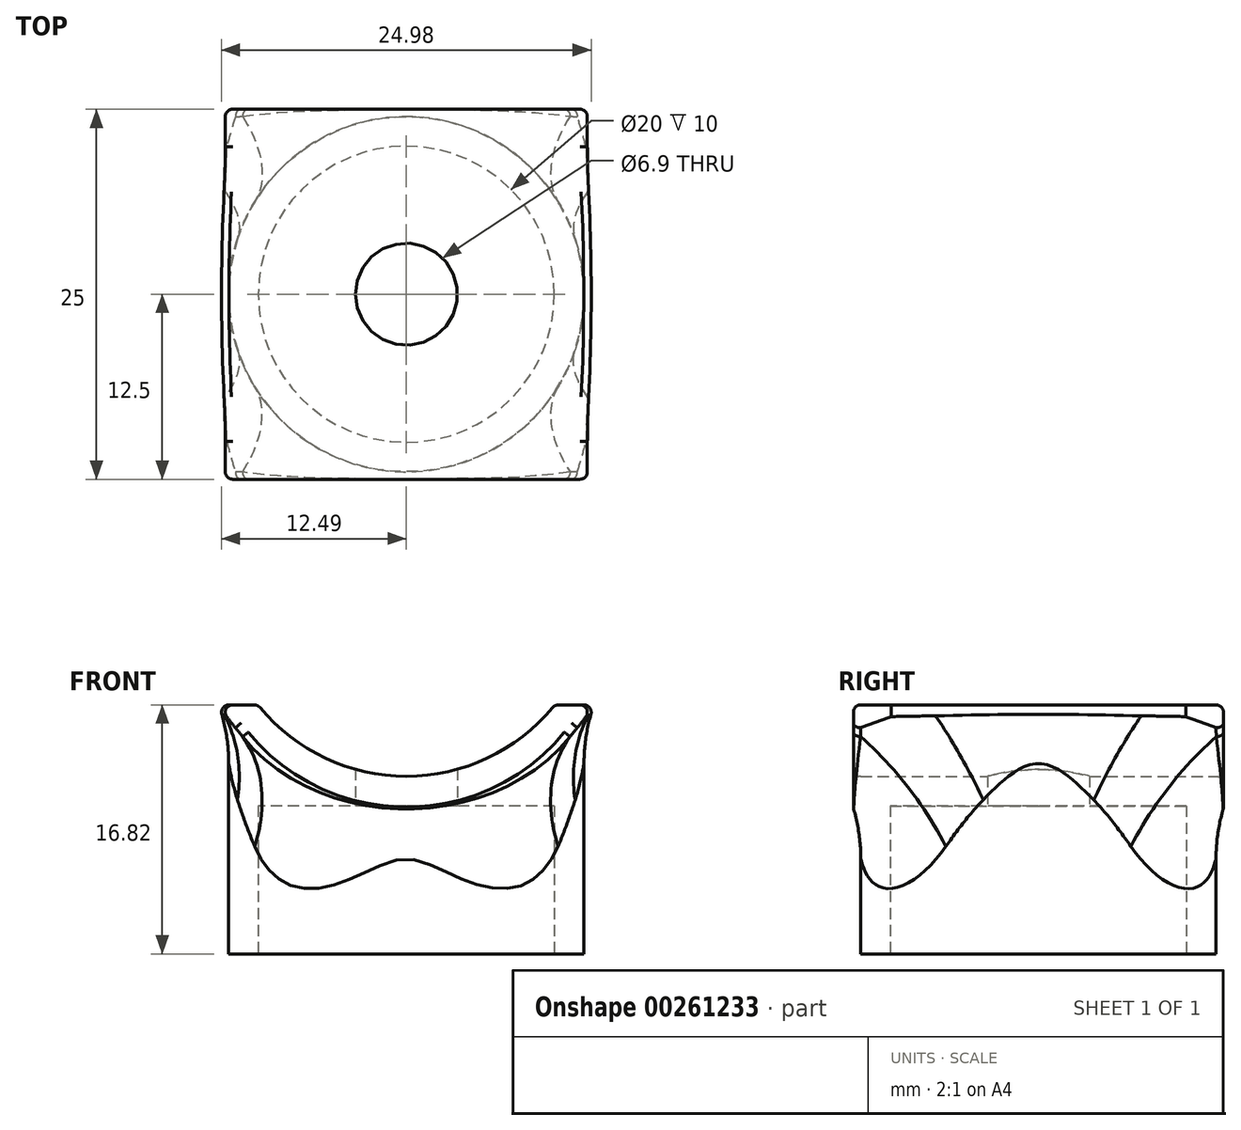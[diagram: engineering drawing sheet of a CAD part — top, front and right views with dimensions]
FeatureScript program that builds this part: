
annotation { "Feature Type Name" : "Feature", "Feature Type Description" : "" }
export const myFeature = defineFeature(function(context is Context, id is Id, definition is map)
    precondition{}
    {
        {
            var Q0;
            Q0=qCreatedBy(makeId("Top.planeOp"),FACE);
            var sketch = newSketch(context, id + "F0", { "sketchPlane" : qUnion([Q0])});
            skCircle(sketch, "E0", {"center": v(0, 0) * mm, "radius": 10 * mm});
            skCircle(sketch, "E1", {"center": v(0, 0) * mm, "radius": 12 * mm});
            skCircle(sketch, "E2", {"center": v(0, 0) * mm, "radius": 3.45 * mm});
            skSolve(sketch);
        }
        {
            var Q0;
            Q0=makeQuery(id+"F0.imprint","IMPRINT",FACE,{"disambiguationData":[TD([[makeQuery(id+"F0.imprint","IMPRINT",EDGE,{"derivedFrom":sQuery(id+"F0.wireOp",EDGE,"E0")}),-1.0]])]});
            var Q1;
            Q1=makeQuery(id+"F0.imprint","IMPRINT",FACE,{"disambiguationData":[TD([[makeQuery(id+"F0.imprint","IMPRINT",EDGE,{"derivedFrom":sQuery(id+"F0.wireOp",EDGE,"E0")}),1.0]])]});
            var Q2;
            Q2=makeQuery(id+"F0.imprint","IMPRINT",FACE,{"disambiguationData":[TD([[makeQuery(id+"F0.imprint","IMPRINT",EDGE,{"derivedFrom":sQuery(id+"F0.wireOp",EDGE,"E2")}),1.0]])]});
            extrude(context, id + "F1", {"entities" : qUnion([Q0, Q1, Q2]), "depth" : 20 * mm});
        }
        {
            var Q0;
            Q0=qCreatedBy(makeId("Front.planeOp"),FACE);
            var sketch = newSketch(context, id + "F2", { "sketchPlane" : qUnion([Q0])});
            skPoint(sketch, "E3.0", {"position": v(0, 24.85) * mm});
            skLineSegment(sketch, "E4", {"start": v(0, 0) * mm, "end": v(0, 24.85) * mm});
            skSolve(sketch);
        }
        {
            var Q0;
            Q0=qCreatedBy(makeId("Front.planeOp"),FACE);
            var sketch = newSketch(context, id + "F3", { "sketchPlane" : qUnion([Q0])});
            skPoint(sketch, "E5.0", {"position": v(0, 24.85) * mm});
            skCircle(sketch, "E6", {"center": v(0, 24.85) * mm, "radius": 12.85 * mm});
            skCircle(sketch, "E7", {"center": v(0, 24.85) * mm, "radius": 15 * mm});
            skSolve(sketch);
        }
        {
            var Q0;
            Q0=makeQuery(id+"F3.imprint","IMPRINT",FACE,{"disambiguationData":[TD([[makeQuery(id+"F3.imprint","IMPRINT",EDGE,{"derivedFrom":sQuery(id+"F3.wireOp",EDGE,"E6")}),-1.0]])]});
            extrude(context, id + "F4", {"entities" : qUnion([Q0]), "operationType" : NewBodyOperationType.ADD, "endBound" : BoundingType.SYMMETRIC, "depth" : 25 * mm});
        }
        {
            var Q0;
            Q0=qCreatedBy(makeId("Front.planeOp"),FACE);
            var sketch = newSketch(context, id + "F5", { "sketchPlane" : qUnion([Q0])});
            skCircle(sketch, "E8.0", {"center": v(0, 24.85) * mm, "radius": 12.85 * mm});
            skSolve(sketch);
        }
        {
            var Q0;
            Q0 = qSketchRegion(id + "F5", true);
            extrude(context, id + "F6", {"entities" : qUnion([Q0]), "operationType" : NewBodyOperationType.REMOVE, "endBound" : BoundingType.SYMMETRIC, "depth" : 27 * mm});
        }
        {
            var Q0;
            Q0=makeQuery(id+"F0.imprint","IMPRINT",FACE,{"disambiguationData":[TD([[makeQuery(id+"F0.imprint","IMPRINT",EDGE,{"derivedFrom":sQuery(id+"F0.wireOp",EDGE,"E0")}),1.0]])]});
            var sketch = newSketch(context, id + "F7", { "sketchPlane" : qUnion([Q0])});
            skSolve(sketch);
        }
        {
            var Q0;
            Q0 = qSketchRegion(id + "F7", true);
            var Q1;
            Q1=makeQuery(id+"F0.imprint","IMPRINT",FACE,{"disambiguationData":[TD([[makeQuery(id+"F0.imprint","IMPRINT",EDGE,{"derivedFrom":sQuery(id+"F0.wireOp",EDGE,"E0")}),1.0]])]});
            extrude(context, id + "F8", {"entities" : qUnion([Q0, Q1]), "operationType" : NewBodyOperationType.REMOVE, "depth" : 10 * mm});
        }
        {
            var Q0;
            Q0=makeQuery(id+"F0.imprint","IMPRINT",FACE,{"disambiguationData":[TD([[makeQuery(id+"F0.imprint","IMPRINT",EDGE,{"derivedFrom":sQuery(id+"F0.wireOp",EDGE,"E2")}),1.0]])]});
            extrude(context, id + "F9", {"entities" : qUnion([Q0]), "operationType" : NewBodyOperationType.REMOVE, "depth" : 13 * mm});
        }
        {
            var Q0;
            Q0=qCreatedBy(makeId("Front.planeOp"),FACE);
            var sketch = newSketch(context, id + "F10", { "sketchPlane" : qUnion([Q0])});
            skLineSegment(sketch, "E9.bottom", {"start": v(-16.9, 16.82) * mm, "end": v(16.45, 16.82) * mm});
            skLineSegment(sketch, "E9.top", {"start": v(-16.9, 40.94) * mm, "end": v(16.45, 40.94) * mm});
            skLineSegment(sketch, "E9.left", {"start": v(-16.9, 16.82) * mm, "end": v(-16.9, 40.94) * mm});
            skLineSegment(sketch, "E9.right", {"start": v(16.45, 16.82) * mm, "end": v(16.45, 40.94) * mm});
            skSolve(sketch);
        }
        {
            var Q0;
            Q0=makeQuery(id+"F10.imprint","IMPRINT",FACE,{"disambiguationData":[TD([[makeQuery(id+"F10.imprint","IMPRINT",EDGE,{"derivedFrom":sQuery(id+"F10.wireOp",EDGE,"E9.bottom")}),1.0]])]});
            extrude(context, id + "F11", {"entities" : qUnion([Q0]), "operationType" : NewBodyOperationType.REMOVE, "endBound" : BoundingType.SYMMETRIC, "oppositeDirection" : true, "depth" : 27 * mm});
        }
        {
            var Q0;
            Q0=makeQuery(id+"F4.boolean.opBoolean","INTERSECT",EDGE,{"derivedFrom":[makeQuery(id+"F1.opExtrude","SWEPT_FACE",FACE,{"disambiguationData":[OSD([sQuery(id+"F0.wireOp",EDGE,"E1")])]}),makeQuery(id+"F4.opExtrude","SWEPT_FACE",FACE,{"disambiguationData":[OSD([sQuery(id+"F3.wireOp",EDGE,"E7")])]})]});
            fillet(context, id + "F12", {"entities" : qUnion([Q0]), "radius" : 12 * mm, "tangentPropagation" : true, "allowEdgeOverflow" : false});
        }
        {
            var Q0;
            Q0=makeQuery(id+"F11.boolean.opBoolean","COPY",FACE,{"disambiguationData":[OD(0.0)],"derivedFrom":makeQuery(id+"F11.opExtrude","SWEPT_FACE",FACE,{"disambiguationData":[OSD([sQuery(id+"F10.wireOp",EDGE,"E9.bottom")])]})});
            var Q1;
            Q1=makeQuery(id+"F4.opExtrude","CAP_FACE",FACE,{"disambiguationData":[OSD([sQuery(id+"F3.wireOp",EDGE,"E6"),sQuery(id+"F3.wireOp",EDGE,"E7")])],"isStart":false});
            var Q2;
            Q2=makeQuery(id+"F11.boolean.opBoolean","COPY",FACE,{"disambiguationData":[OD(1.0)],"derivedFrom":makeQuery(id+"F11.opExtrude","SWEPT_FACE",FACE,{"disambiguationData":[OSD([sQuery(id+"F10.wireOp",EDGE,"E9.bottom")])]})});
            var Q3;
            Q3=makeQuery(id+"F4.opExtrude","CAP_FACE",FACE,{"disambiguationData":[OSD([sQuery(id+"F3.wireOp",EDGE,"E6"),sQuery(id+"F3.wireOp",EDGE,"E7")])],"isStart":true});
            fillet(context, id + "F13", {"entities" : qUnion([Q0, Q1, Q2, Q3]), "radius" : .5 * mm, "tangentPropagation" : true, "allowEdgeOverflow" : false});
        }
    });
